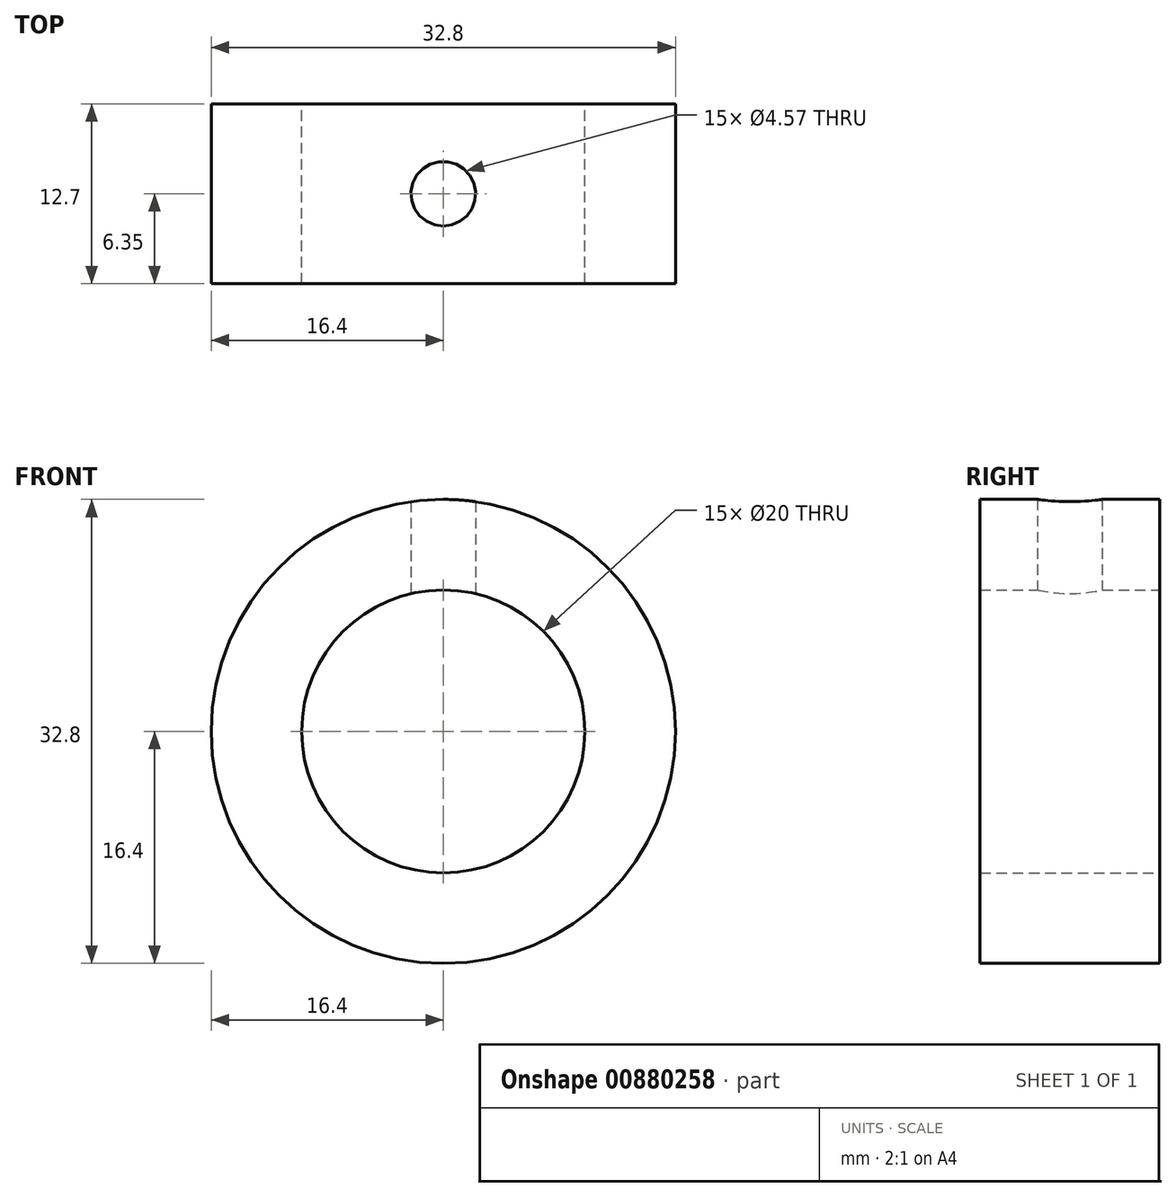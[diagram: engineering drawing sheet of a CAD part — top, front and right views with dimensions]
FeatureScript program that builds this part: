
annotation { "Feature Type Name" : "Feature", "Feature Type Description" : "" }
export const myFeature = defineFeature(function(context is Context, id is Id, definition is map)
    precondition{}
    {
        {
            var Q0;
            Q0=qCreatedBy(makeId("Front.planeOp"),FACE);
            var sketch = newSketch(context, id + "F0", { "sketchPlane" : qUnion([Q0])});
            skCircle(sketch, "E0", {"center": v(0, 0) * mm, "radius": 10 * mm});
            skCircle(sketch, "E1", {"center": v(0, 0) * mm, "radius": 16.4 * mm});
            skSolve(sketch);
        }
        {
            var Q0;
            Q0=qSketchRegion(id+"F0",true);
            extrude(context, id + "F1", {"entities" : qUnion([Q0]), "depth" : 12.7 * mm});
        }
        {
            var Q0;
            Q0=qCreatedBy(makeId("Top.planeOp"),FACE);
            var sketch = newSketch(context, id + "F2", { "sketchPlane" : qUnion([Q0])});
            skCircle(sketch, "E2", {"center": v(0, -6.35) * mm, "radius": 2.29 * mm});
            skSolve(sketch);
        }
        {
            var Q0;
            Q0=makeQuery(id+"F2.imprint","IMPRINT",FACE,{"disambiguationData":[TD([[makeQuery(id+"F2.imprint","IMPRINT",EDGE,{"derivedFrom":sQuery(id+"F2.wireOp",EDGE,"E2")}),1.0]])]});
            extrude(context, id + "F3", {"entities" : qUnion([Q0]), "operationType" : NewBodyOperationType.REMOVE, "depth" : 25.4 * mm});
        }
    });
